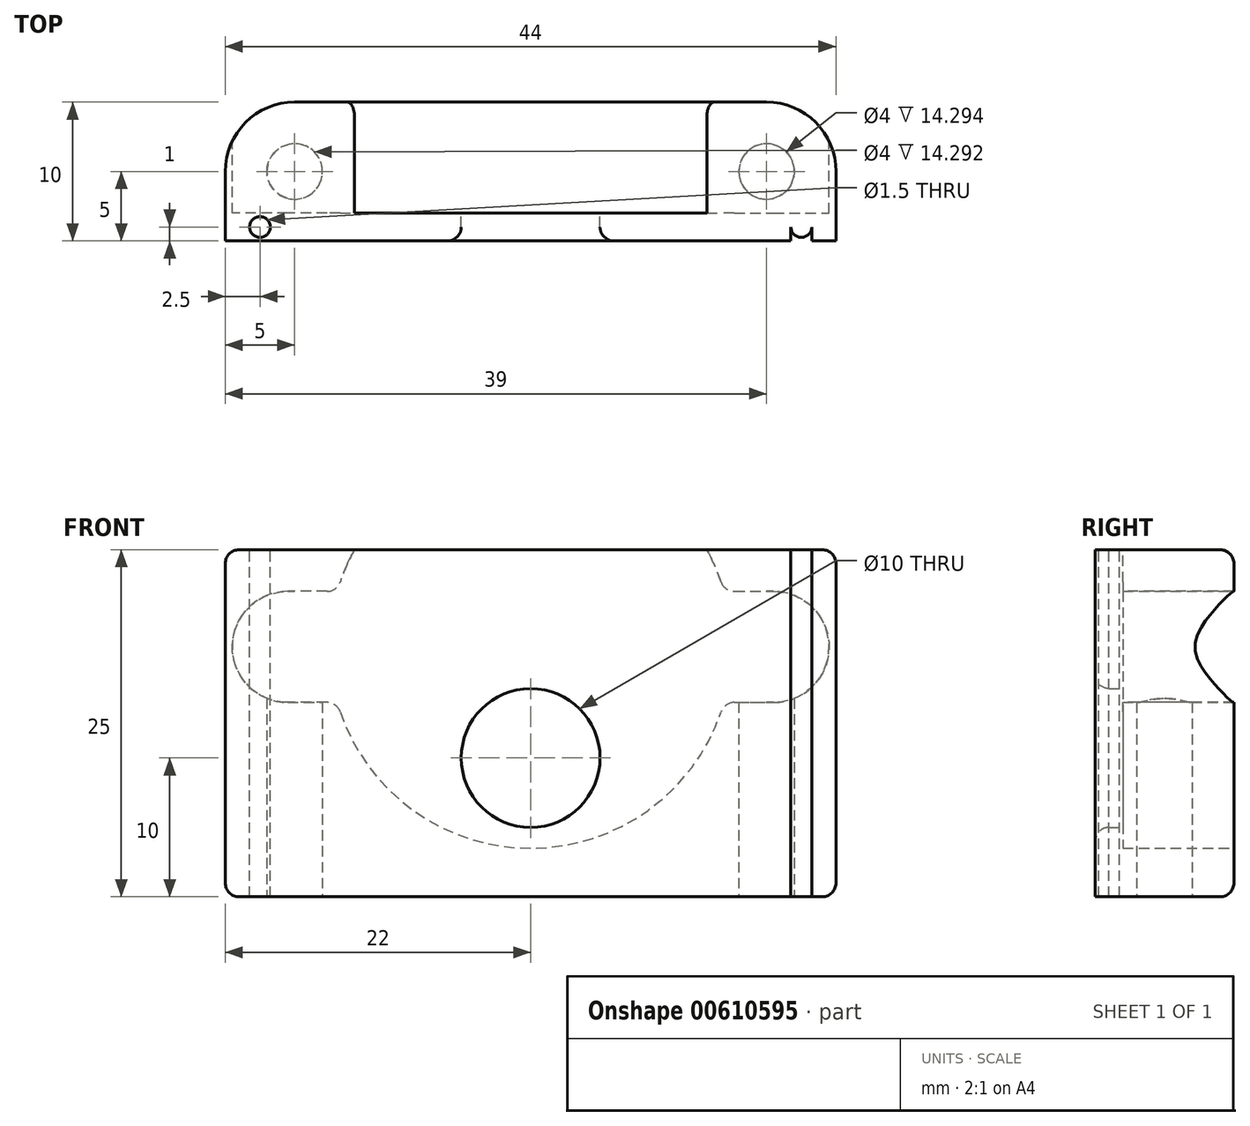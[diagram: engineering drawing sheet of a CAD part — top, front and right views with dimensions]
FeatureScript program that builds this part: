
annotation { "Feature Type Name" : "Feature", "Feature Type Description" : "" }
export const myFeature = defineFeature(function(context is Context, id is Id, definition is map)
    precondition{}
    {
        {
            var Q0;
            Q0=qCreatedBy(makeId("Top.planeOp"),FACE);
            var sketch = newSketch(context, id + "F0", { "sketchPlane" : qUnion([Q0])});
            skLineSegment(sketch, "E0", {"start": v(0, 0) * mm, "end": v(0, 20) * mm, "construction": true});
            skLineSegment(sketch, "E1", {"start": v(0, 10) * mm, "end": v(-22, 10) * mm});
            skLineSegment(sketch, "E2", {"start": v(-22, 10) * mm, "end": v(-22, 0) * mm});
            skLineSegment(sketch, "E3", {"start": v(-22, 0) * mm, "end": v(0, 0) * mm});
            skLineSegment(sketch, "E4", {"start": v(-22, 0) * mm, "end": v(-37, -25) * mm});
            skLineSegment(sketch, "E5", {"start": v(-37, -25) * mm, "end": v(-27, -25) * mm});
            skLineSegment(sketch, "E6", {"start": v(-27, -25) * mm, "end": v(-17, 0) * mm});
            skLineSegment(sketch, "E7", {"start": v(-22, 5) * mm, "end": v(-3.26, 5) * mm, "construction": true});
            skPoint(sketch, "E8", {"position": v(-17, 5) * mm});
            skLineSegment(sketch, "E9.MirrorCS", {"start": v(0, 10) * mm, "end": v(22, 10) * mm});
            skLineSegment(sketch, "E10.MirrorCS", {"start": v(22, 10) * mm, "end": v(22, 0) * mm});
            skPoint(sketch, "E11.MirrorP", {"position": v(17, 5) * mm});
            skLineSegment(sketch, "E12.MirrorCS", {"start": v(22, 0) * mm, "end": v(0, 0) * mm});
            skLineSegment(sketch, "E13.MirrorCS", {"start": v(27, -25) * mm, "end": v(17, 0) * mm});
            skLineSegment(sketch, "E14.MirrorCS", {"start": v(22, 0) * mm, "end": v(37, -25) * mm});
            skLineSegment(sketch, "E15.MirrorCS", {"start": v(37, -25) * mm, "end": v(27, -25) * mm});
            skSolve(sketch);
        }
        {
            var Q0;
            Q0=makeQuery(id+"F0.imprint","IMPRINT",FACE,{"disambiguationData":[TD([[makeQuery(id+"F0.imprint","IMPRINT",EDGE,{"derivedFrom":sQuery(id+"F0.wireOp",EDGE,"E1")}),1.0]])]});
            extrude(context, id + "F1", {"entities" : qUnion([Q0]), "depth" : 25 * mm, "offsetDistance" : 25 * mm});
        }
        {
            var Q0;
            Q0=sQuery(id+"F0.wireOp",VERTEX,"E8");
            var Q1;
            Q1=sQuery(id+"F0.wireOp",VERTEX,"E11.MirrorP");
            var Q2;
            Q2=makeQuery(id+"F1.opExtrude","SWEPT_BODY",BODY,{"disambiguationData":[OSD([sQuery(id+"F0.wireOp",EDGE,"E1"),sQuery(id+"F0.wireOp",EDGE,"E2"),sQuery(id+"F0.wireOp",EDGE,"E3"),sQuery(id+"F0.wireOp",EDGE,"E4"),sQuery(id+"F0.wireOp",EDGE,"E5"),sQuery(id+"F0.wireOp",EDGE,"E6"),sQuery(id+"F0.wireOp",EDGE,"E9.MirrorCS"),sQuery(id+"F0.wireOp",EDGE,"E10.MirrorCS"),sQuery(id+"F0.wireOp",EDGE,"E12.MirrorCS"),sQuery(id+"F0.wireOp",EDGE,"E13.MirrorCS"),sQuery(id+"F0.wireOp",EDGE,"E14.MirrorCS"),sQuery(id+"F0.wireOp",EDGE,"E15.MirrorCS")])]});
            hole(context, id + "F2", {"style" : HoleStyle.SIMPLE, "endStyle" : HoleEndStyle.BLIND, "oppositeDirection" : true, "holeDiameter" : 4 * mm, "majorDiameter" : 5 * mm, "holeDepth" : 17 * mm, "isTappedThrough" : true, "tappedDepth" : 12 * mm, "tapClearance" : 3, "locations" : qUnion([Q0, Q1]), "scope" : qUnion([Q2])});
        }
        {
            var Q0;
            Q0=makeQuery(id+"F1.opExtrude","SWEPT_FACE",FACE,{"disambiguationData":[OSD([sQuery(id+"F0.wireOp",EDGE,"E1"),sQuery(id+"F0.wireOp",EDGE,"E9.MirrorCS")])]});
            var sketch = newSketch(context, id + "F3", { "sketchPlane" : qUnion([Q0])});
            skCircle(sketch, "E16", {"center": v(0, 18) * mm, "radius": 14.5 * mm});
            skPoint(sketch, "E16.centerSnap0", {"position": v(0, 25) * mm});
            skLineSegment(sketch, "E17", {"start": v(0, 18) * mm, "end": v(19.21, 18) * mm, "construction": true});
            skCircle(sketch, "E18", {"center": v(17.5, 18) * mm, "radius": 2.08 * mm});
            skLineSegment(sketch, "E19", {"start": v(13.94, 22) * mm, "end": v(17.5, 22) * mm});
            skLineSegment(sketch, "E20.MirrorCS", {"start": v(13.94, 14) * mm, "end": v(17.5, 14) * mm});
            skArc(sketch, "E21", {"start": v(17.5, 22) * mm, "mid": v(21.5, 18) * mm, "end": v(17.5, 14) * mm});
            skLineSegment(sketch, "E22", {"start": v(0, 18) * mm, "end": v(0, 30.5) * mm, "construction": true});
            skCircle(sketch, "E23.MirrorC", {"center": v(-17.5, 18) * mm, "radius": 2.08 * mm});
            skArc(sketch, "E24.MirrorCS", {"start": v(-17.5, 22) * mm, "mid": v(-21.5, 18) * mm, "end": v(-17.5, 14) * mm});
            skLineSegment(sketch, "E25.MirrorCS", {"start": v(-13.94, 22) * mm, "end": v(-17.5, 22) * mm});
            skLineSegment(sketch, "E26.MirrorCS", {"start": v(-13.94, 14) * mm, "end": v(-17.5, 14) * mm});
            skCircle(sketch, "E27", {"center": v(0, 10) * mm, "radius": 5 * mm});
            skSolve(sketch);
        }
        {
            var Q0;
            Q0=makeQuery(id+"F3.imprint","IMPRINT",FACE,{"disambiguationData":[TD([[makeQuery(id+"F3.imprint","IMPRINT",EDGE,{"derivedFrom":sQuery(id+"F3.wireOp",EDGE,"E27")}),1.0]])]});
            extrude(context, id + "F4", {"entities" : qUnion([Q0]), "operationType" : NewBodyOperationType.REMOVE, "endBound" : BoundingType.THROUGH_ALL, "oppositeDirection" : true, "depth" : 25 * mm, "offsetDistance" : 25 * mm});
        }
        {
            var Q0;
            Q0=makeQuery(id+"F3.imprint","IMPRINT",FACE,{"disambiguationData":[TD([[makeQuery(id+"F3.imprint","IMPRINT",EDGE,{"derivedFrom":sQuery(id+"F3.wireOp",EDGE,"E18")}),-1.0]])]});
            var Q1;
            Q1=makeQuery(id+"F3.imprint","IMPRINT",FACE,{"disambiguationData":[TD([[makeQuery(id+"F3.imprint","IMPRINT",EDGE,{"derivedFrom":sQuery(id+"F3.wireOp",EDGE,"E27")}),-1.0]])]});
            var Q2;
            Q2=makeQuery(id+"F3.imprint","IMPRINT",FACE,{"disambiguationData":[TD([[makeQuery(id+"F3.imprint","IMPRINT",EDGE,{"derivedFrom":sQuery(id+"F3.wireOp",EDGE,"E23.MirrorC")}),1.0]])]});
            var Q3;
            Q3=makeQuery(id+"F3.imprint","IMPRINT",FACE,{"disambiguationData":[TD([[makeQuery(id+"F3.imprint","IMPRINT",EDGE,{"derivedFrom":sQuery(id+"F3.wireOp",EDGE,"E18")}),1.0]])]});
            var Q4;
            Q4=makeQuery(id+"F3.imprint","IMPRINT",FACE,{"disambiguationData":[TD([[makeQuery(id+"F3.imprint","IMPRINT",EDGE,{"derivedFrom":sQuery(id+"F3.wireOp",EDGE,"E23.MirrorC")}),-1.0]])]});
            extrude(context, id + "F5", {"entities" : qUnion([Q0, Q1, Q2, Q3, Q4]), "operationType" : NewBodyOperationType.REMOVE, "oppositeDirection" : true, "depth" : 8 * mm, "offsetDistance" : 25 * mm});
        }
        {
            var Q0;
            Q0=makeQuery(id+"F1.opExtrude","SWEPT_EDGE",EDGE,{"disambiguationData":[OSD([sQuery(id+"F0.wireOp",EDGE,"E1"),sQuery(id+"F0.wireOp",EDGE,"E2")])]});
            var Q1;
            Q1=makeQuery(id+"F1.opExtrude","SWEPT_EDGE",EDGE,{"disambiguationData":[OSD([sQuery(id+"F0.wireOp",EDGE,"E9.MirrorCS"),sQuery(id+"F0.wireOp",EDGE,"E10.MirrorCS")])]});
            fillet(context, id + "F6", {"entities" : qUnion([Q0, Q1]), "radius" : 5 * mm, "tangentPropagation" : true, "allowEdgeOverflow" : false});
        }
        {
            var Q0;
            Q0=makeQuery(id+"F1.opExtrude","CAP_FACE",FACE,{"disambiguationData":[OSD([sQuery(id+"F0.wireOp",EDGE,"E1"),sQuery(id+"F0.wireOp",EDGE,"E2"),sQuery(id+"F0.wireOp",EDGE,"E3"),sQuery(id+"F0.wireOp",EDGE,"E9.MirrorCS"),sQuery(id+"F0.wireOp",EDGE,"E10.MirrorCS"),sQuery(id+"F0.wireOp",EDGE,"E12.MirrorCS")])],"isStart":false});
            var sketch = newSketch(context, id + "F7", { "sketchPlane" : qUnion([Q0])});
            skLineSegment(sketch, "E28.bottom", {"start": v(-20.25, 0) * mm, "end": v(-18.75, 0) * mm});
            skLineSegment(sketch, "E28.top", {"start": v(-20.25, 1) * mm, "end": v(-18.75, 1) * mm});
            skLineSegment(sketch, "E28.left", {"start": v(-20.25, 0) * mm, "end": v(-20.25, 1) * mm});
            skLineSegment(sketch, "E28.right", {"start": v(-18.75, 0) * mm, "end": v(-18.75, 1) * mm});
            skCircle(sketch, "E29", {"center": v(-19.5, 1) * mm, "radius": 0.75 * mm});
            skCircle(sketch, "E30.MirrorC", {"center": v(19.5, 1) * mm, "radius": 0.75 * mm});
            skLineSegment(sketch, "E31.MirrorCS", {"start": v(20.25, 0) * mm, "end": v(20.25, 1) * mm});
            skLineSegment(sketch, "E32.MirrorCS", {"start": v(18.75, 0) * mm, "end": v(18.75, 1) * mm});
            skLineSegment(sketch, "E33.MirrorCS", {"start": v(20.25, 0) * mm, "end": v(18.75, 0) * mm});
            skSolve(sketch);
        }
        {
            var Q0;
            {var subQ0=sQuery(id+"F7.wireOp",EDGE,"E28.top");Q0=makeQuery(id+"F7.imprint","IMPRINT",FACE,{"disambiguationData":[TD([[makeQuery(id+"F7.imprint","IMPRINT",EDGE,{"derivedFrom":subQ0}),1.0]])]});}
            var Q1;
            {var subQ0=sQuery(id+"F7.wireOp",EDGE,"E28.top");Q1=makeQuery(id+"F7.imprint","IMPRINT",FACE,{"disambiguationData":[TD([[makeQuery(id+"F7.imprint","IMPRINT",EDGE,{"derivedFrom":subQ0}),-1.0]])]});}
            var Q2;
            Q2=makeQuery(id+"F7.imprint","IMPRINT",FACE,{"disambiguationData":[TD([[makeQuery(id+"F7.imprint","IMPRINT",EDGE,{"derivedFrom":sQuery(id+"F7.wireOp",EDGE,"E28.bottom")}),-1.0]])]});
            var Q3;
            {var subQ0=sQuery(id+"F7.wireOp",EDGE,"E30.MirrorC");var subQ1=makeQuery(id+"F7.imprint","INTERSECT",VERTEX,{"derivedFrom":[subQ0,sQuery(id+"F7.wireOp",EDGE,"E31.MirrorCS")]});Q3=makeQuery(id+"F7.imprint","IMPRINT",FACE,{"disambiguationData":[TD([[makeQuery(id+"F7.imprint","IMPRINT",EDGE,{"disambiguationData":[TD([[subQ1,1.0]])],"derivedFrom":subQ0}),-1.0]])]});}
            var Q4;
            {var subQ0=sQuery(id+"F7.wireOp",EDGE,"E31.MirrorCS");Q4=makeQuery(id+"F7.imprint","IMPRINT",FACE,{"disambiguationData":[TD([[makeQuery(id+"F7.imprint","IMPRINT",EDGE,{"derivedFrom":subQ0}),1.0]])]});}
            extrude(context, id + "F8", {"entities" : qUnion([Q0, Q1, Q2, Q3, Q4]), "operationType" : NewBodyOperationType.REMOVE, "endBound" : BoundingType.THROUGH_ALL, "oppositeDirection" : true, "depth" : 25 * mm, "offsetDistance" : 25 * mm});
        }
        {
            var Q0;
            Q0=makeQuery(id+"F4.boolean.opBoolean","INTERSECT",EDGE,{"derivedFrom":[makeQuery(id+"F1.opExtrude","SWEPT_FACE",FACE,{"disambiguationData":[OSD([sQuery(id+"F0.wireOp",EDGE,"E3"),sQuery(id+"F0.wireOp",EDGE,"E12.MirrorCS")])]}),makeQuery(id+"F4.opExtrude","SWEPT_FACE",FACE,{"disambiguationData":[OSD([sQuery(id+"F3.wireOp",EDGE,"E27")])]})]});
            var Q1;
            Q1=makeQuery(id+"F5.boolean.opBoolean","COPY",EDGE,{"derivedFrom":makeQuery(id+"F5.opExtrude","CAP_EDGE",EDGE,{"disambiguationData":[OSD([sQuery(id+"F3.wireOp",EDGE,"E27")])],"isStart":false})});
            var Q2;
            Q2=makeQuery(id+"F2.hole-0.boolean.opBoolean","COPY",EDGE,{"derivedFrom":makeQuery(id+"F2.hole-0.opRevolve","SWEPT_EDGE",EDGE,{"disambiguationData":[OSD([sQuery(id+"F2.hole-0.sketch.wireOp",EDGE,"core_line_2"),sQuery(id+"F2.hole-0.sketch.wireOp",EDGE,"core_line_3")])]})});
            var Q3;
            {var subQ0=sQuery(id+"F3.wireOp",EDGE,"E16");Q3=makeQuery(id+"F5.boolean.opBoolean","COPY",EDGE,{"derivedFrom":makeQuery(id+"F5.opExtrude","CAP_EDGE",EDGE,{"disambiguationData":[OSD([subQ0]),TDD([makeQuery(id+"F3.imprint","IMPRINT",EDGE,{"disambiguationData":[TD([[makeQuery(id+"F3.imprint","INTERSECT",VERTEX,{"derivedFrom":[subQ0,sQuery(id+"F3.wireOp",EDGE,"E20.MirrorCS")]}),1.0]])],"derivedFrom":subQ0})])],"isStart":true})});}
            var Q4;
            {var subQ0=sQuery(id+"F3.wireOp",EDGE,"E16");Q4=makeQuery(id+"F5.boolean.opBoolean","COPY",EDGE,{"derivedFrom":makeQuery(id+"F5.opExtrude","CAP_EDGE",EDGE,{"disambiguationData":[OSD([subQ0]),TDD([makeQuery(id+"F3.imprint","IMPRINT",EDGE,{"disambiguationData":[TD([[makeQuery(id+"F3.imprint","INTERSECT",VERTEX,{"derivedFrom":[subQ0,sQuery(id+"F3.wireOp",EDGE,"E25.MirrorCS")]}),1.0]])],"derivedFrom":subQ0})])],"isStart":true})});}
            var Q5;
            {var subQ0=sQuery(id+"F3.wireOp",EDGE,"E16");Q5=makeQuery(id+"F5.boolean.opBoolean","COPY",EDGE,{"derivedFrom":makeQuery(id+"F5.opExtrude","CAP_EDGE",EDGE,{"disambiguationData":[OSD([subQ0]),TDD([makeQuery(id+"F3.imprint","IMPRINT",EDGE,{"disambiguationData":[TD([[makeQuery(id+"F3.imprint","INTERSECT",VERTEX,{"derivedFrom":[subQ0,sQuery(id+"F3.wireOp",EDGE,"E19")]}),-1.0]])],"derivedFrom":subQ0})])],"isStart":true})});}
            var Q6;
            Q6=makeQuery(id+"F2.hole-1.boolean.opBoolean","COPY",EDGE,{"derivedFrom":makeQuery(id+"F2.hole-1.opRevolve","SWEPT_EDGE",EDGE,{"disambiguationData":[OSD([sQuery(id+"F2.hole-1.sketch.wireOp",EDGE,"core_line_2"),sQuery(id+"F2.hole-1.sketch.wireOp",EDGE,"core_line_3")])]})});
            var Q7;
            Q7=makeQuery(id+"F1.opExtrude","CAP_EDGE",EDGE,{"disambiguationData":[OSD([sQuery(id+"F0.wireOp",EDGE,"E1"),sQuery(id+"F0.wireOp",EDGE,"E9.MirrorCS")])],"isStart":true});
            var Q8;
            {var subQ0=sQuery(id+"F0.wireOp",EDGE,"E10.MirrorCS");var subQ1=sQuery(id+"F0.wireOp",EDGE,"E9.MirrorCS");Q8=makeQuery(id+"F6.opFillet","BLEND_EDGE",EDGE,{"blendedFrom":[makeQuery(id+"F1.opExtrude","SWEPT_EDGE",EDGE,{"disambiguationData":[OSD([subQ1,subQ0])]}),makeQuery(id+"F1.opExtrude","CAP_FACE",FACE,{"disambiguationData":[OSD([sQuery(id+"F0.wireOp",EDGE,"E1"),sQuery(id+"F0.wireOp",EDGE,"E2"),sQuery(id+"F0.wireOp",EDGE,"E3"),subQ1,subQ0,sQuery(id+"F0.wireOp",EDGE,"E12.MirrorCS")])],"isStart":false})],"blendedInto":[makeQuery(id+"F1.opExtrude","CAP_FACE",FACE,{"disambiguationData":[OSD([sQuery(id+"F0.wireOp",EDGE,"E1"),sQuery(id+"F0.wireOp",EDGE,"E2"),sQuery(id+"F0.wireOp",EDGE,"E3"),subQ1,subQ0,sQuery(id+"F0.wireOp",EDGE,"E12.MirrorCS")])],"isStart":false})]});}
            var Q9;
            {var subQ0=sQuery(id+"F0.wireOp",EDGE,"E2");var subQ1=sQuery(id+"F0.wireOp",EDGE,"E1");Q9=makeQuery(id+"F6.opFillet","BLEND_EDGE",EDGE,{"blendedFrom":[makeQuery(id+"F1.opExtrude","SWEPT_EDGE",EDGE,{"disambiguationData":[OSD([subQ1,subQ0])]}),makeQuery(id+"F1.opExtrude","CAP_FACE",FACE,{"disambiguationData":[OSD([subQ1,subQ0,sQuery(id+"F0.wireOp",EDGE,"E3"),sQuery(id+"F0.wireOp",EDGE,"E9.MirrorCS"),sQuery(id+"F0.wireOp",EDGE,"E10.MirrorCS"),sQuery(id+"F0.wireOp",EDGE,"E12.MirrorCS")])],"isStart":false})],"blendedInto":[makeQuery(id+"F1.opExtrude","CAP_FACE",FACE,{"disambiguationData":[OSD([subQ1,subQ0,sQuery(id+"F0.wireOp",EDGE,"E3"),sQuery(id+"F0.wireOp",EDGE,"E9.MirrorCS"),sQuery(id+"F0.wireOp",EDGE,"E10.MirrorCS"),sQuery(id+"F0.wireOp",EDGE,"E12.MirrorCS")])],"isStart":false})]});}
            var Q10;
            Q10=makeQuery(id+"F5.boolean.opBoolean","COPY",EDGE,{"derivedFrom":makeQuery(id+"F5.opExtrude","SWEPT_EDGE",EDGE,{"disambiguationData":[OSD([sQuery(id+"F3.wireOp",EDGE,"E16"),sQuery(id+"F3.wireOp",EDGE,"E25.MirrorCS")])]})});
            var Q11;
            Q11=makeQuery(id+"F5.boolean.opBoolean","COPY",EDGE,{"derivedFrom":makeQuery(id+"F5.opExtrude","SWEPT_EDGE",EDGE,{"disambiguationData":[OSD([sQuery(id+"F3.wireOp",EDGE,"E16"),sQuery(id+"F3.wireOp",EDGE,"E26.MirrorCS")])]})});
            var Q12;
            Q12=makeQuery(id+"F5.boolean.opBoolean","COPY",EDGE,{"derivedFrom":makeQuery(id+"F5.opExtrude","SWEPT_EDGE",EDGE,{"disambiguationData":[OSD([sQuery(id+"F3.wireOp",EDGE,"E16"),sQuery(id+"F3.wireOp",EDGE,"E20.MirrorCS")])]})});
            var Q13;
            Q13=makeQuery(id+"F5.boolean.opBoolean","COPY",EDGE,{"derivedFrom":makeQuery(id+"F5.opExtrude","SWEPT_EDGE",EDGE,{"disambiguationData":[OSD([sQuery(id+"F3.wireOp",EDGE,"E16"),sQuery(id+"F3.wireOp",EDGE,"E19")])]})});
            var Q14;
            {var subQ0=sQuery(id+"F3.wireOp",EDGE,"E16");var subQ1=sQuery(id+"F0.wireOp",EDGE,"E9.MirrorCS");var subQ2=sQuery(id+"F0.wireOp",EDGE,"E1");Q14=makeQuery(id+"F5.boolean.opBoolean","COPY",EDGE,{"derivedFrom":makeQuery(id+"F5.opExtrude","SWEPT_EDGE",EDGE,{"disambiguationData":[OSD([subQ2,subQ1,subQ0]),TDD([makeQuery(id+"F3.imprint","INTERSECT",VERTEX,{"disambiguationData":[OD(0.0)],"derivedFrom":[makeQuery(id+"F1.opExtrude","CAP_EDGE",EDGE,{"disambiguationData":[OSD([subQ2,subQ1])],"isStart":false}),subQ0]})])]})});}
            var Q15;
            {var subQ0=sQuery(id+"F3.wireOp",EDGE,"E16");var subQ1=sQuery(id+"F0.wireOp",EDGE,"E9.MirrorCS");var subQ2=sQuery(id+"F0.wireOp",EDGE,"E1");Q15=makeQuery(id+"F5.boolean.opBoolean","COPY",EDGE,{"derivedFrom":makeQuery(id+"F5.opExtrude","SWEPT_EDGE",EDGE,{"disambiguationData":[OSD([subQ2,subQ1,subQ0]),TDD([makeQuery(id+"F3.imprint","INTERSECT",VERTEX,{"disambiguationData":[OD(1.0)],"derivedFrom":[makeQuery(id+"F1.opExtrude","CAP_EDGE",EDGE,{"disambiguationData":[OSD([subQ2,subQ1])],"isStart":false}),subQ0]})])]})});}
            var Q16;
            Q16=makeQuery(id+"F5.boolean.opBoolean","COPY",EDGE,{"derivedFrom":makeQuery(id+"F5.opExtrude","CAP_EDGE",EDGE,{"disambiguationData":[OSD([sQuery(id+"F0.wireOp",EDGE,"E1"),sQuery(id+"F0.wireOp",EDGE,"E9.MirrorCS")])],"isStart":false})});
            fillet(context, id + "F9", {"entities" : qUnion([Q0, Q1, Q2, Q3, Q4, Q5, Q6, Q7, Q8, Q9, Q10, Q11, Q12, Q13, Q14, Q15, Q16]), "radius" : 1 * mm, "tangentPropagation" : true, "allowEdgeOverflow" : false});
        }
    });
